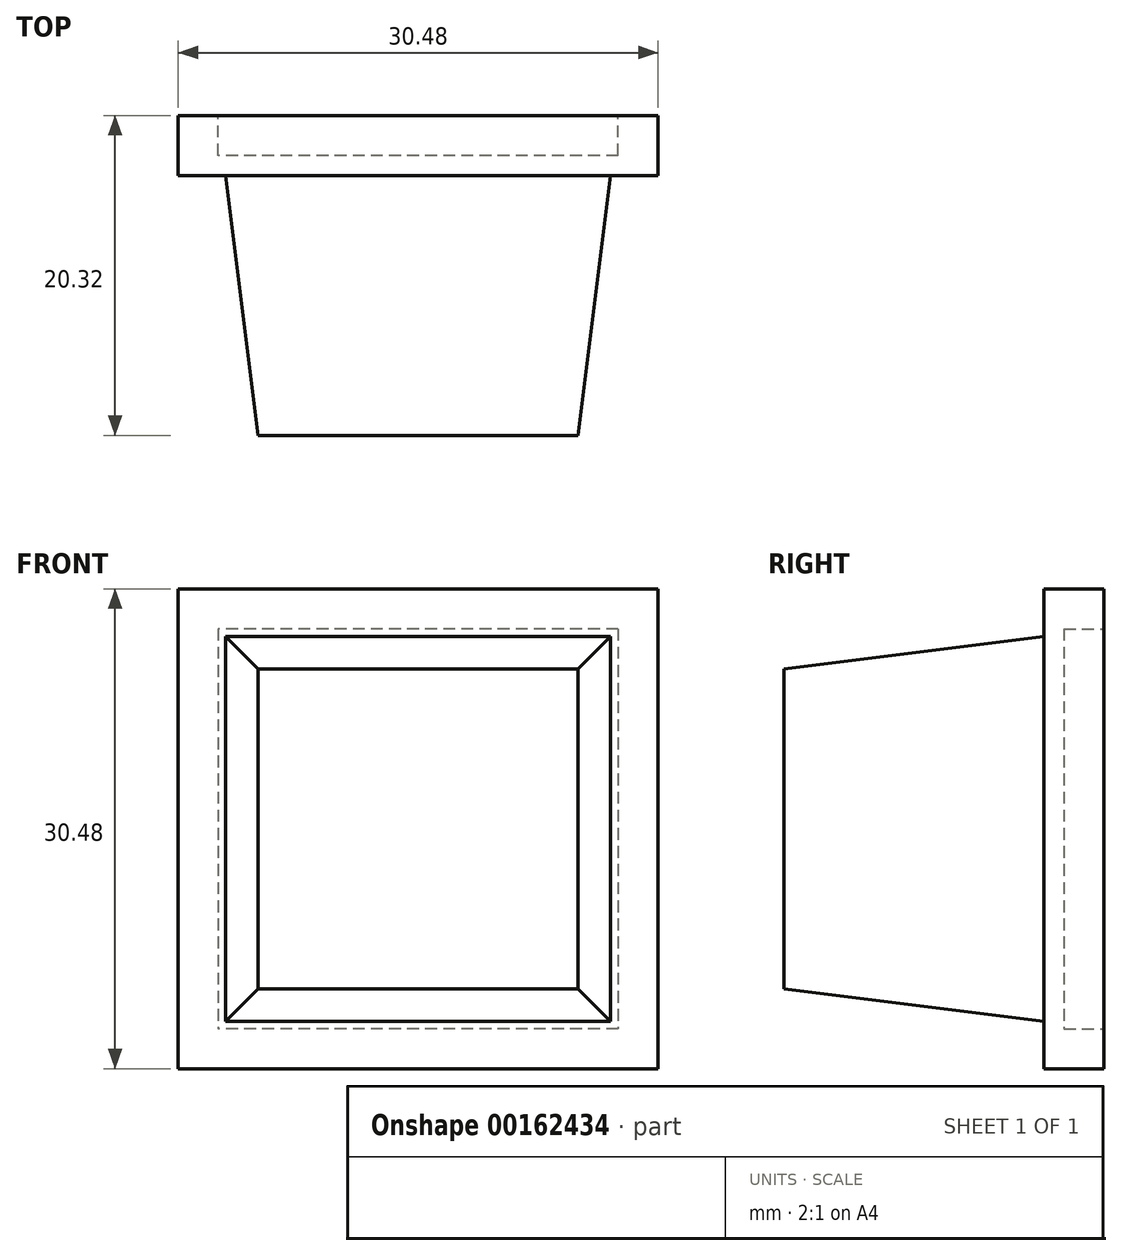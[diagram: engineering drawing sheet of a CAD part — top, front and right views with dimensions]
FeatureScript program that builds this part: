
annotation { "Feature Type Name" : "Feature", "Feature Type Description" : "" }
export const myFeature = defineFeature(function(context is Context, id is Id, definition is map)
    precondition{}
    {
        {
            var Q0;
            Q0=qCreatedBy(makeId("Front.planeOp"),FACE);
            var sketch = newSketch(context, id + "F0", { "sketchPlane" : qUnion([Q0])});
            skLineSegment(sketch, "E0.bottom", {"start": v(15.24, 15.24) * mm, "end": v(-15.24, 15.24) * mm});
            skLineSegment(sketch, "E0.top", {"start": v(15.24, -15.24) * mm, "end": v(-15.24, -15.24) * mm});
            skLineSegment(sketch, "E0.left", {"start": v(15.24, 15.24) * mm, "end": v(15.24, -15.24) * mm});
            skLineSegment(sketch, "E0.right", {"start": v(-15.24, 15.24) * mm, "end": v(-15.24, -15.24) * mm});
            skPoint(sketch, "E0.middle", {"position": v(0, 0) * mm});
            skLineSegment(sketch, "E1.bottom", {"start": v(12.7, 12.7) * mm, "end": v(-12.7, 12.7) * mm});
            skLineSegment(sketch, "E1.top", {"start": v(12.7, -12.7) * mm, "end": v(-12.7, -12.7) * mm});
            skLineSegment(sketch, "E1.left", {"start": v(12.7, 12.7) * mm, "end": v(12.7, -12.7) * mm});
            skLineSegment(sketch, "E1.right", {"start": v(-12.7, 12.7) * mm, "end": v(-12.7, -12.7) * mm});
            skLineSegment(sketch, "E2.bottom", {"start": v(7.62, 7.62) * mm, "end": v(-7.62, 7.62) * mm});
            skLineSegment(sketch, "E2.top", {"start": v(7.62, -7.62) * mm, "end": v(-7.62, -7.62) * mm});
            skLineSegment(sketch, "E2.left", {"start": v(7.62, 7.62) * mm, "end": v(7.62, -7.62) * mm});
            skLineSegment(sketch, "E2.right", {"start": v(-7.62, 7.62) * mm, "end": v(-7.62, -7.62) * mm});
            skSolve(sketch);
        }
        {
            var Q0;
            Q0=makeQuery(id+"F0.imprint","IMPRINT",FACE,{"disambiguationData":[TD([[makeQuery(id+"F0.imprint","IMPRINT",EDGE,{"derivedFrom":sQuery(id+"F0.wireOp",EDGE,"E0.bottom")}),1.0]])]});
            extrude(context, id + "F1", {"entities" : qUnion([Q0]), "depth" : 3.8 * mm});
        }
        {
            var Q0;
            Q0=makeQuery(id+"F0.imprint","IMPRINT",FACE,{"disambiguationData":[TD([[makeQuery(id+"F0.imprint","IMPRINT",EDGE,{"derivedFrom":sQuery(id+"F0.wireOp",EDGE,"E1.bottom")}),1.0]])]});
            var Q1;
            Q1=makeQuery(id+"F0.imprint","IMPRINT",FACE,{"disambiguationData":[TD([[makeQuery(id+"F0.imprint","IMPRINT",EDGE,{"derivedFrom":sQuery(id+"F0.wireOp",EDGE,"E2.bottom")}),1.0]])]});
            extrude(context, id + "F2", {"entities" : qUnion([Q0, Q1]), "operationType" : NewBodyOperationType.ADD, "depth" : 20.32 * mm});
        }
        {
            var Q0;
            Q0=makeQuery(id+"F0.imprint","IMPRINT",FACE,{"disambiguationData":[TD([[makeQuery(id+"F0.imprint","IMPRINT",EDGE,{"derivedFrom":sQuery(id+"F0.wireOp",EDGE,"E1.bottom")}),1.0]])]});
            var Q1;
            Q1=makeQuery(id+"F0.imprint","IMPRINT",FACE,{"disambiguationData":[TD([[makeQuery(id+"F0.imprint","IMPRINT",EDGE,{"derivedFrom":sQuery(id+"F0.wireOp",EDGE,"E2.bottom")}),1.0]])]});
            extrude(context, id + "F3", {"entities" : qUnion([Q0, Q1]), "operationType" : NewBodyOperationType.REMOVE, "depth" : 2.54 * mm});
        }
        {
            var Q0;
            Q0=makeQuery(id+"F2.opExtrude","CAP_EDGE",EDGE,{"disambiguationData":[OSD([sQuery(id+"F0.wireOp",EDGE,"E1.bottom")])],"isStart":false});
            var Q1;
            Q1=makeQuery(id+"F2.opExtrude","CAP_EDGE",EDGE,{"disambiguationData":[OSD([sQuery(id+"F0.wireOp",EDGE,"E1.right")])],"isStart":false});
            var Q2;
            Q2=makeQuery(id+"F2.opExtrude","CAP_EDGE",EDGE,{"disambiguationData":[OSD([sQuery(id+"F0.wireOp",EDGE,"E1.top")])],"isStart":false});
            var Q3;
            Q3=makeQuery(id+"F2.opExtrude","CAP_EDGE",EDGE,{"disambiguationData":[OSD([sQuery(id+"F0.wireOp",EDGE,"E1.left")])],"isStart":false});
            chamfer(context, id + "F4", {"entities" : qUnion([Q0, Q1, Q2, Q3]), "chamferType" : ChamferType.TWO_OFFSETS, "width1" : 2.54 * mm, "oppositeDirection" : false, "width2" : 20.32 * mm, "tangentPropagation" : true});
        }
    });
